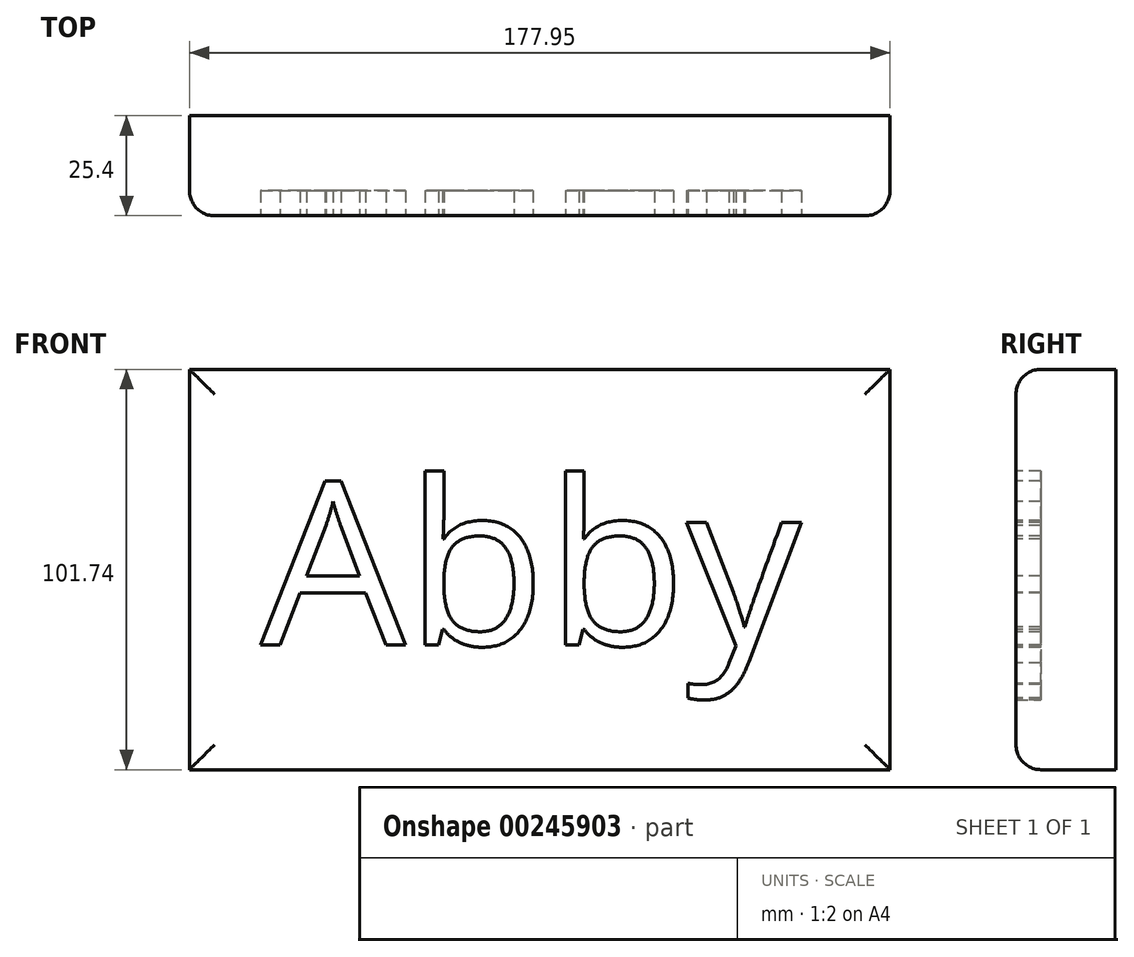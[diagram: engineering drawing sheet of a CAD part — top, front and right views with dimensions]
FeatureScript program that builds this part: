
annotation { "Feature Type Name" : "Feature", "Feature Type Description" : "" }
export const myFeature = defineFeature(function(context is Context, id is Id, definition is map)
    precondition{}
    {
        {
            var Q0;
            Q0=qCreatedBy(makeId("Front.planeOp"),FACE);
            var sketch = newSketch(context, id + "F0", { "sketchPlane" : qUnion([Q0])});
            skLineSegment(sketch, "E0", {"start": v(-76.58, 67.84) * mm, "end": v(101.37, 67.84) * mm});
            skLineSegment(sketch, "E1", {"start": v(101.37, 67.84) * mm, "end": v(101.37, -33.9) * mm});
            skLineSegment(sketch, "E2", {"start": v(101.37, -33.9) * mm, "end": v(-76.58, -33.9) * mm});
            skLineSegment(sketch, "E3", {"start": v(-76.58, -33.9) * mm, "end": v(-76.58, 67.84) * mm});
            skSolve(sketch);
        }
        {
            var Q0;
            Q0=makeQuery(id+"F0.imprint","IMPRINT",FACE,{"disambiguationData":[TD([[makeQuery(id+"F0.imprint","IMPRINT",EDGE,{"derivedFrom":sQuery(id+"F0.wireOp",EDGE,"E0")}),-1.0]])]});
            extrude(context, id + "F1", {"entities" : qUnion([Q0]), "depth" : 25.4 * mm});
        }
        {
            var Q0;
            Q0=makeQuery(id+"F1.opExtrude","CAP_FACE",FACE,{"disambiguationData":[OSD([sQuery(id+"F0.wireOp",EDGE,"E0"),sQuery(id+"F0.wireOp",EDGE,"E1"),sQuery(id+"F0.wireOp",EDGE,"E2"),sQuery(id+"F0.wireOp",EDGE,"E3")])],"isStart":false});
            fillet(context, id + "F2", {"entities" : qUnion([Q0]), "radius" : 6.35 * mm, "tangentPropagation" : true, "allowEdgeOverflow" : false});
        }
        {
            var Q0;
            Q0=makeQuery(id+"F1.opExtrude","CAP_FACE",FACE,{"disambiguationData":[OSD([sQuery(id+"F0.wireOp",EDGE,"E0"),sQuery(id+"F0.wireOp",EDGE,"E1"),sQuery(id+"F0.wireOp",EDGE,"E2"),sQuery(id+"F0.wireOp",EDGE,"E3")])],"isStart":false});
            var sketch = newSketch(context, id + "F3", { "sketchPlane" : qUnion([Q0])});
            skText(sketch, "E4", { "text": "Abby", "fontName": "OpenSans-Regular.ttf"});
            const initialGuessF3  = {"E4": [-0.05851, -0.00222, 1, 0, 0.04189]};
            skSetInitialGuess(sketch, initialGuessF3);
            skSolve(sketch);
        }
        {
            var Q0;
            Q0 = qSketchRegion(id + "F3", true);
            extrude(context, id + "F4", {"entities" : qUnion([Q0]), "operationType" : NewBodyOperationType.REMOVE, "oppositeDirection" : true, "depth" : 6.35 * mm});
        }
    });
